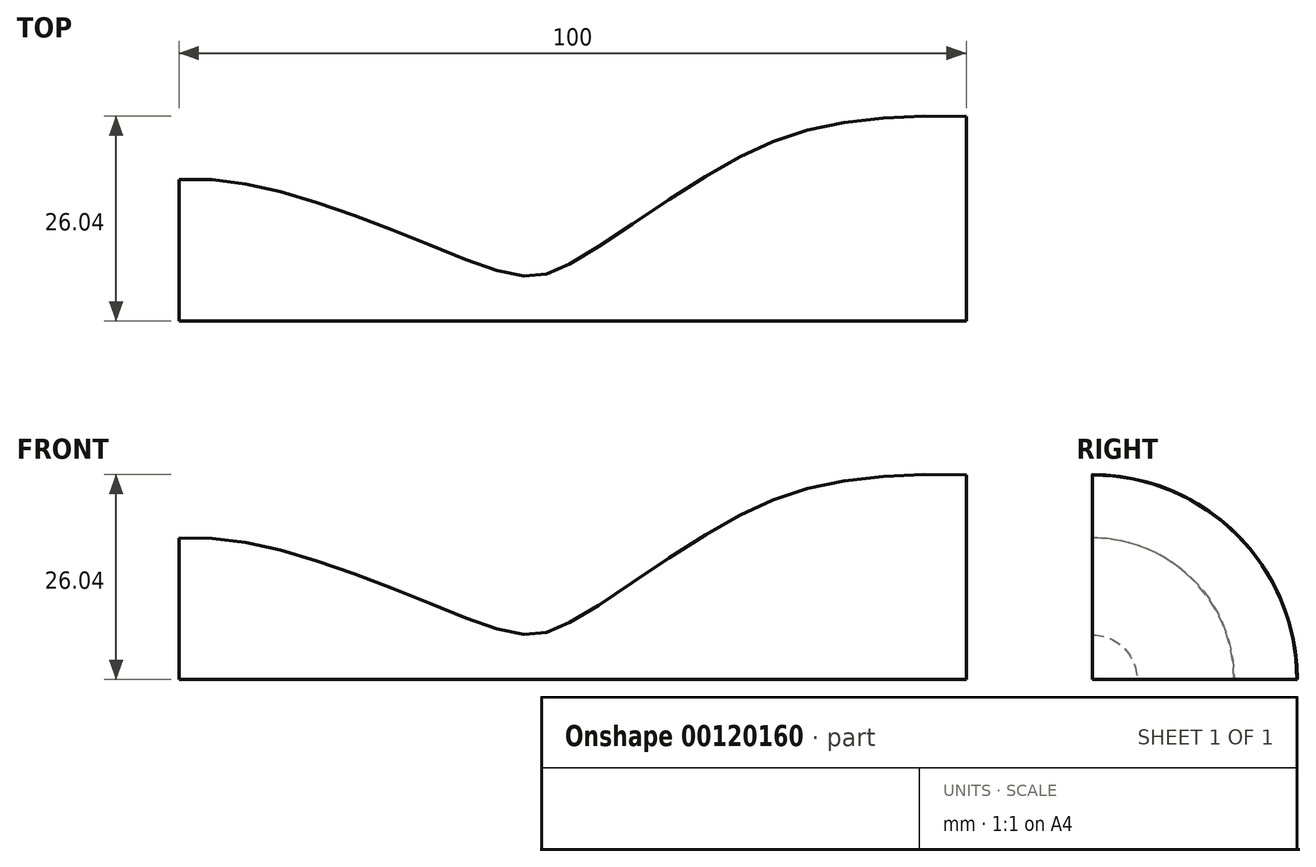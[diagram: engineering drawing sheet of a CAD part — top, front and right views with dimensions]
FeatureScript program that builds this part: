
annotation { "Feature Type Name" : "Feature", "Feature Type Description" : "" }
export const myFeature = defineFeature(function(context is Context, id is Id, definition is map)
    precondition{}
    {
        {
            var Q0;
            Q0=qCreatedBy(makeId("Top.planeOp"),FACE);
            var sketch = newSketch(context, id + "F0", { "sketchPlane" : qUnion([Q0])});
            skFitSpline(sketch, "E0", {"points": [v(0, 18) * mm, v(13.5, 16.27) * mm, v(31.05, 9.98) * mm, v(43.62, 5.73) * mm, v(49.9, 7.4) * mm, v(66.17, 17.93) * mm, v(81.15, 24.58) * mm, v(100, 26) * mm], "startDerivative": vector(95.95, 4.4) * mm, "endDerivative": vector(122.76, -2.58) * mm});
            skLineSegment(sketch, "E1", {"start": v(0, 18) * mm, "end": v(0, 0) * mm});
            skLineSegment(sketch, "E2", {"start": v(0, 0) * mm, "end": v(100, 0) * mm});
            skLineSegment(sketch, "E3", {"start": v(100, 0) * mm, "end": v(100, 26) * mm});
            skSolve(sketch);
        }
        {
            var Q0;
            Q0=makeQuery(id+"F0.imprint","IMPRINT",FACE,{"disambiguationData":[TD([[makeQuery(id+"F0.imprint","IMPRINT",EDGE,{"derivedFrom":sQuery(id+"F0.wireOp",EDGE,"E0")}),-1.0]])]});
            var Q1;
            Q1=sQuery(id+"F0.wireOp",EDGE,"E2");
            revolve(context, id + "F1", {"entities" : qUnion([Q0]), "axis" : qUnion([Q1]), "revolveType" : RevolveType.ONE_DIRECTION, "angle" : 90 * degree});
        }
    });
